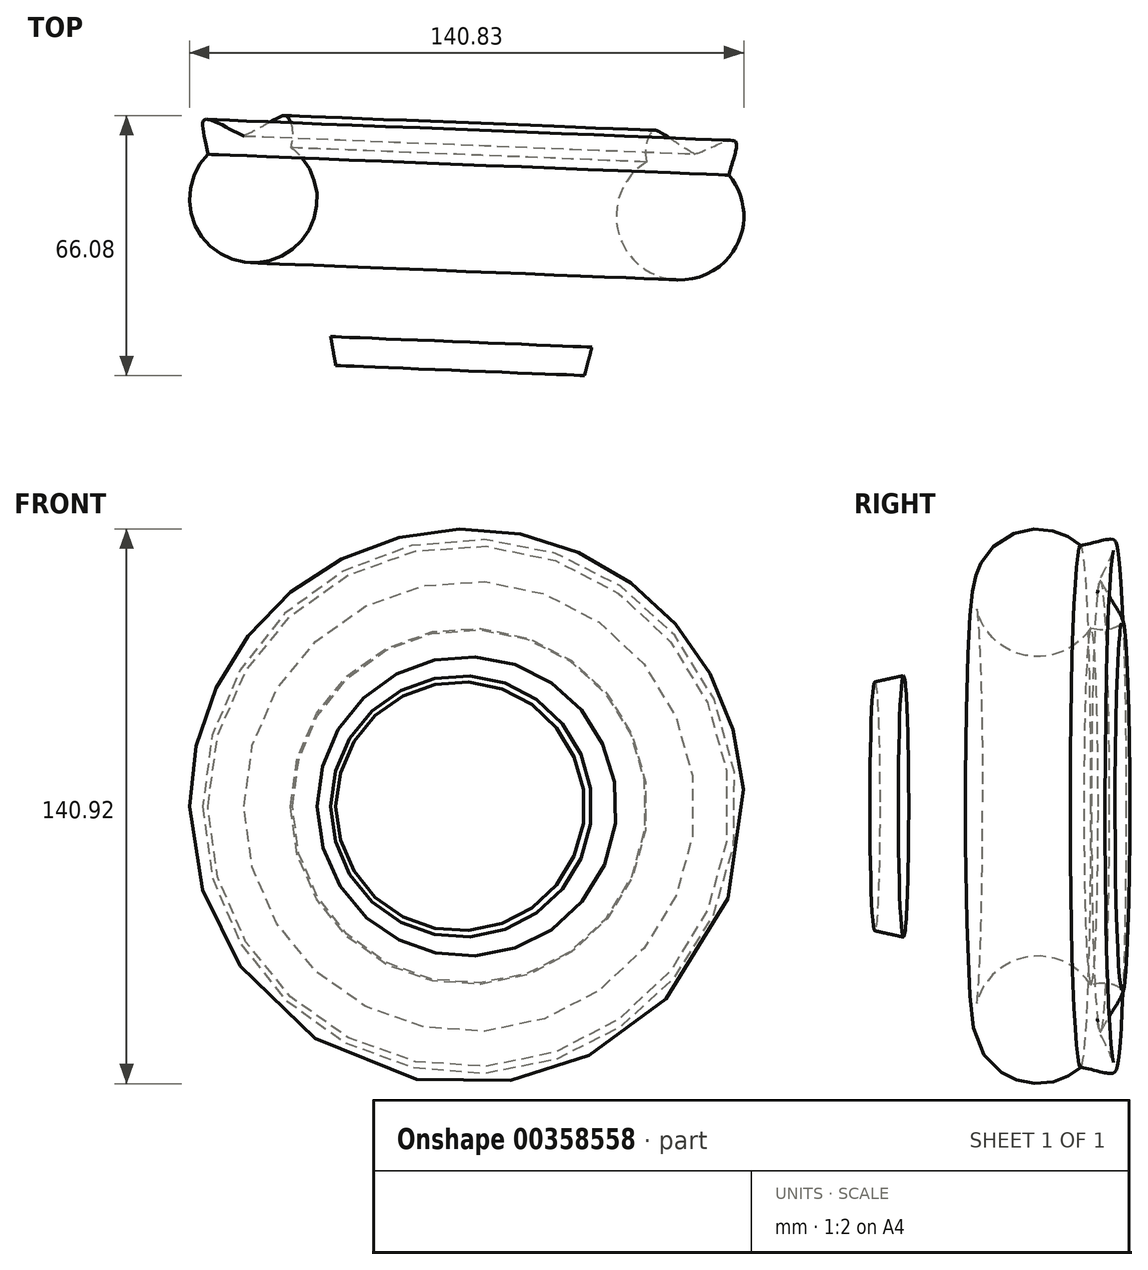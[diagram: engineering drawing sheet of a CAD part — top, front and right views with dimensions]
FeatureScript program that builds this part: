
annotation { "Feature Type Name" : "Feature", "Feature Type Description" : "" }
export const myFeature = defineFeature(function(context is Context, id is Id, definition is map)
    precondition{}
    {
        {
            var Q0;
            Q0=qCreatedBy(makeId("Top.planeOp"),FACE);
            var sketch = newSketch(context, id + "F0", { "sketchPlane" : qUnion([Q0])});
            skCircle(sketch, "E0", {"center": v(-35.66, 24.74) * mm, "radius": 16.2 * mm});
            skFitSpline(sketch, "E1", {"points": [v(-47.21, 36.1) * mm, v(-47.7, 44.97) * mm, v(-38.03, 40.77) * mm, v(-37.85, 40.8) * mm], "startDerivative": vector(-4.27, 30.62) * mm, "endDerivative": vector(-4.5, 0.57) * mm});
            skFitSpline(sketch, "E2", {"points": [v(-33.28, 40.77) * mm, v(-29.2, 45.45) * mm, v(-27.25, 45.83) * mm, v(-26.2, 37.9) * mm], "startDerivative": vector(1.21, 24.84) * mm, "endDerivative": vector(-8.18, -28.53) * mm});
            skFitSpline(sketch, "E3", {"points": [v(-35.66, 24.74) * mm, v(-38.84, 21.85) * mm, v(-42.36, 22.29) * mm, v(-41.8, 22.14) * mm, v(-41.66, 22.14) * mm], "startDerivative": vector(-5.1, -9.78) * mm, "endDerivative": vector(1.2, 0.28) * mm});
            skFitSpline(sketch, "E4", {"points": [v(-35.66, 24.74) * mm, v(-34.33, 22.14) * mm, v(-28.7, 22.14) * mm], "startDerivative": vector(2.6, -7.36) * mm, "endDerivative": vector(11.48, 1.75) * mm});
            skFitSpline(sketch, "E5", {"points": [v(-36.6, 14.86) * mm, v(-36.77, 15.34) * mm], "startDerivative": vector(-0.16, 0.48) * mm, "endDerivative": vector(-0.16, 0.48) * mm});
            skFitSpline(sketch, "E6", {"points": [v(-47.94, 14.61) * mm, v(-48.48, 14.83) * mm, v(-50.97, 13.52) * mm, v(-50.97, 13.52) * mm, v(-59.4, -20.44) * mm], "startDerivative": vector(6.61, 11.52) * mm, "endDerivative": vector(3.6, -60.9) * mm});
            skFitSpline(sketch, "E7", {"points": [v(-42.55, -6.57) * mm, v(-43.7, -7.73) * mm, v(-45.52, -7.56) * mm, v(-45.86, -6.9) * mm, v(-46.35, -5.9) * mm, v(-46.35, -5.08) * mm, v(-46.52, 0) * mm], "startDerivative": vector(-5.41, -8.68) * mm, "endDerivative": vector(-1.18, 21.24) * mm});
            skFitSpline(sketch, "E8", {"points": [v(-42.55, -6.57) * mm, v(-42.55, 0) * mm], "startDerivative": vector(0, 6.57) * mm, "endDerivative": vector(0, 6.57) * mm});
            skFitSpline(sketch, "E9", {"points": [v(-38.74, 0) * mm, v(-38.58, -3.43) * mm, v(-38.58, -5.25) * mm, v(-38.58, -5.75) * mm], "startDerivative": vector(0.46, -7.59) * mm, "endDerivative": vector(0.01, -2.36) * mm});
            skFitSpline(sketch, "E10", {"points": [v(-38.78, -5.01) * mm, v(-37.6, -7.35) * mm, v(-36.41, -7.77) * mm, v(-35.27, -7.39) * mm, v(-34.73, -6.28) * mm, v(-34.77, -5.73) * mm, v(-34.77, -4.75) * mm, v(-34.78, -3.6) * mm, v(-34.6, -2.27) * mm, v(-34.6, 0) * mm], "startDerivative": vector(2.49, -9.3) * mm, "endDerivative": vector(-0.54, 15.38) * mm});
            skFitSpline(sketch, "E11", {"points": [v(-59.4, -20.44) * mm, v(-13.77, -23.01) * mm], "startDerivative": vector(44.57, 2.95) * mm, "endDerivative": vector(44.57, 2.95) * mm});
            skFitSpline(sketch, "E12", {"points": [v(-26.4, 11.44) * mm, v(-21.8, 9.2) * mm, v(-13.77, -23.01) * mm], "startDerivative": vector(17.15, -2.76) * mm, "endDerivative": vector(10.06, -58.07) * mm});
            skPoint(sketch, "E13.1.internal.orphan", {"position": v(3.74, -23.01) * mm});
            skCircle(sketch, "E14", {"center": v(-39.54, 31.27) * mm, "radius": 0.29 * mm});
            skCircle(sketch, "E15", {"center": v(-31.27, 30.78) * mm, "radius": 0.33 * mm});
            skFitSpline(sketch, "E16", {"points": [v(-13.77, -23.01) * mm, v(-16.18, -9.11) * mm], "startDerivative": vector(-2.24, 13.9) * mm, "endDerivative": vector(-2.24, 13.9) * mm});
            skFitSpline(sketch, "E17", {"points": [v(-15.43, -13.75) * mm, v(-10.07, -10.74) * mm, v(-10.34, -9.94) * mm, v(-11.41, 4.3) * mm, v(-6.04, 9.93) * mm, v(0, -16.92) * mm, v(-14.51, -18.38) * mm], "startDerivative": vector(57.96, 27.76) * mm, "endDerivative": vector(-92.43, 23.5) * mm});
            skPoint(sketch, "E18.start.orphan", {"position": v(0, 57.45) * mm});
            skLineSegment(sketch, "E19", {"start": v(20.13, 61.88) * mm, "end": v(16.44, -30.21) * mm});
            skSolve(sketch);
        }
        {
            var Q0;
            {var subQ0=sQuery(id+"F0.wireOp",EDGE,"E2");Q0=makeQuery(id+"F0.imprint","IMPRINT",FACE,{"disambiguationData":[TD([[makeQuery(id+"F0.imprint","IMPRINT",EDGE,{"derivedFrom":subQ0}),-1.0]])]});}
            var Q1;
            {var subQ0=sQuery(id+"F0.wireOp",EDGE,"E1");var subQ1=sQuery(id+"F0.wireOp",EDGE,"E0");var subQ2=makeQuery(id+"F0.imprint","INTERSECT",VERTEX,{"disambiguationData":[OD(0.0)],"derivedFrom":[subQ1,subQ0]});Q1=makeQuery(id+"F0.imprint","IMPRINT",FACE,{"disambiguationData":[TD([[makeQuery(id+"F0.imprint","IMPRINT",EDGE,{"disambiguationData":[TD([[subQ2,1.0]])],"derivedFrom":subQ1}),-1.0]])]});}
            var Q2;
            {var subQ5=sQuery(id+"F0.wireOp",EDGE,"E11");Q2=makeQuery(id+"F0.imprint","IMPRINT",FACE,{"disambiguationData":[TD([[makeQuery(id+"F0.imprint","IMPRINT",EDGE,{"derivedFrom":subQ5}),1.0]])]});}
            var Q3;
            Q3=makeQuery(id+"F0.imprint","IMPRINT",FACE,{"disambiguationData":[TD([[makeQuery(id+"F0.imprint","IMPRINT",EDGE,{"derivedFrom":sQuery(id+"F0.wireOp",EDGE,"E14")}),-1.0]])]});
            var Q4;
            {var subQ0=sQuery(id+"F0.wireOp",EDGE,"E16");var subQ1=sQuery(id+"F0.wireOp",EDGE,"E12");var subQ3=makeQuery(id+"F0.imprint","INTERSECT",VERTEX,{"disambiguationData":[OD(1.0)],"derivedFrom":[subQ1,subQ0]});Q4=makeQuery(id+"F0.imprint","IMPRINT",FACE,{"disambiguationData":[TD([[makeQuery(id+"F0.imprint","IMPRINT",EDGE,{"disambiguationData":[TD([[subQ3,-1.0]])],"derivedFrom":subQ1}),1.0]])]});}
            var Q5;
            Q5=makeQuery(id+"F0.imprint","IMPRINT",FACE,{"disambiguationData":[TD([[makeQuery(id+"F0.imprint","IMPRINT",EDGE,{"derivedFrom":sQuery(id+"F0.wireOp",EDGE,"E14")}),1.0]])]});
            var Q6;
            Q6=makeQuery(id+"F0.imprint","IMPRINT",FACE,{"disambiguationData":[TD([[makeQuery(id+"F0.imprint","IMPRINT",EDGE,{"derivedFrom":sQuery(id+"F0.wireOp",EDGE,"E15")}),1.0]])]});
            var Q7;
            {var subQ0=sQuery(id+"F0.wireOp",EDGE,"E17");var subQ1=sQuery(id+"F0.wireOp",EDGE,"E12");var subQ2=makeQuery(id+"F0.imprint","INTERSECT",VERTEX,{"derivedFrom":[subQ1,subQ0]});Q7=makeQuery(id+"F0.imprint","IMPRINT",FACE,{"disambiguationData":[TD([[makeQuery(id+"F0.imprint","IMPRINT",EDGE,{"disambiguationData":[TD([[subQ2,1.0]])],"derivedFrom":subQ1}),-1.0]])]});}
            var Q8;
            {var subQ0=sQuery(id+"F0.wireOp",EDGE,"E17");var subQ1=sQuery(id+"F0.wireOp",EDGE,"E12");var subQ2=makeQuery(id+"F0.imprint","INTERSECT",VERTEX,{"derivedFrom":[subQ1,subQ0]});Q8=makeQuery(id+"F0.imprint","IMPRINT",FACE,{"disambiguationData":[TD([[makeQuery(id+"F0.imprint","IMPRINT",EDGE,{"disambiguationData":[TD([[subQ2,-1.0]])],"derivedFrom":subQ1}),-1.0]])]});}
            var Q9;
            {var subQ0=sQuery(id+"F0.wireOp",EDGE,"E1");var subQ1=sQuery(id+"F0.wireOp",EDGE,"E0");var subQ2=makeQuery(id+"F0.imprint","INTERSECT",VERTEX,{"disambiguationData":[OD(1.0)],"derivedFrom":[subQ1,subQ0]});Q9=makeQuery(id+"F0.imprint","IMPRINT",FACE,{"disambiguationData":[TD([[makeQuery(id+"F0.imprint","IMPRINT",EDGE,{"disambiguationData":[TD([[subQ2,-1.0]])],"derivedFrom":subQ1}),1.0]])]});}
            var Q10;
            Q10=sQuery(id+"F0.wireOp",EDGE,"E19");
            revolve(context, id + "F1", {"entities" : qUnion([Q0, Q1, Q2, Q3, Q4, Q5, Q6, Q7, Q8, Q9]), "axis" : qUnion([Q10]), "revolveType" : RevolveType.FULL});
        }
        {
            var Q0;
            {var subQ0=sQuery(id+"F0.wireOp",EDGE,"E2");var subQ1=sQuery(id+"F0.wireOp",EDGE,"E0");Q0=makeQuery(id+"F1.opRevolve","SWEPT_EDGE",EDGE,{"disambiguationData":[OSD([subQ1,subQ0]),TDD([makeQuery(id+"F0.imprint","INTERSECT",VERTEX,{"disambiguationData":[OD(0.0)],"derivedFrom":[subQ1,subQ0]})])]});}
            fillet(context, id + "F2", {"entities" : qUnion([Q0]), "radius" : 76.33 * mm, "tangentPropagation" : true, "allowEdgeOverflow" : false});
        }
    });
